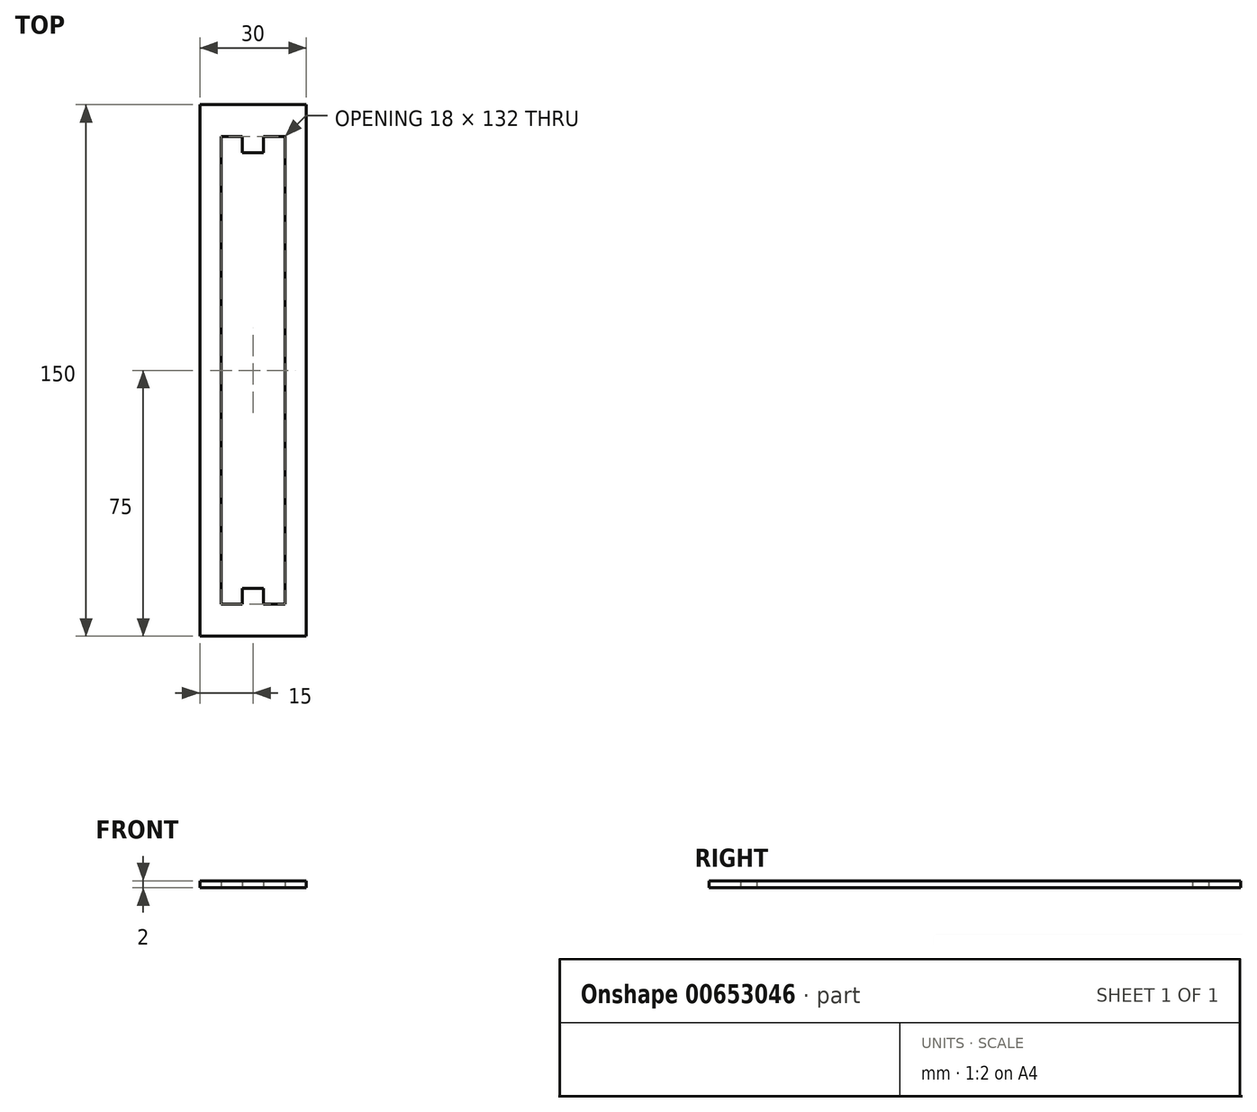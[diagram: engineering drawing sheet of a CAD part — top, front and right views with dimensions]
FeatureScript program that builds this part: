
annotation { "Feature Type Name" : "Feature", "Feature Type Description" : "" }
export const myFeature = defineFeature(function(context is Context, id is Id, definition is map)
    precondition{}
    {
        {
            var Q0;
            Q0=qCreatedBy(makeId("Top.planeOp"),FACE);
            var sketch = newSketch(context, id + "F0", { "sketchPlane" : qUnion([Q0])});
            skLineSegment(sketch, "E0.bottom", {"start": v(0, 0) * mm, "end": v(30, 0) * mm});
            skLineSegment(sketch, "E0.top", {"start": v(0, 150) * mm, "end": v(30, 150) * mm});
            skLineSegment(sketch, "E0.left", {"start": v(0, 0) * mm, "end": v(0, 150) * mm});
            skLineSegment(sketch, "E0.right", {"start": v(30, 0) * mm, "end": v(30, 150) * mm});
            skLineSegment(sketch, "E1", {"start": v(6, 141) * mm, "end": v(12, 141) * mm});
            skLineSegment(sketch, "E2", {"start": v(24, 141) * mm, "end": v(24, 9) * mm});
            skLineSegment(sketch, "E3", {"start": v(6, 141) * mm, "end": v(6, 9) * mm});
            skLineSegment(sketch, "E4", {"start": v(6, 9) * mm, "end": v(12, 9) * mm});
            skLineSegment(sketch, "E5", {"start": v(18, 141) * mm, "end": v(18, 136.5) * mm});
            skLineSegment(sketch, "E6", {"start": v(18, 136.5) * mm, "end": v(12, 136.5) * mm});
            skLineSegment(sketch, "E7", {"start": v(12, 136.5) * mm, "end": v(12, 141) * mm});
            skLineSegment(sketch, "E8", {"start": v(12, 9) * mm, "end": v(12, 13.5) * mm});
            skLineSegment(sketch, "E9", {"start": v(12, 13.5) * mm, "end": v(18, 13.5) * mm});
            skLineSegment(sketch, "E10", {"start": v(18, 13.5) * mm, "end": v(18, 9) * mm});
            skLineSegment(sketch, "E11.trimOffspring", {"start": v(18, 9) * mm, "end": v(24, 9) * mm});
            skLineSegment(sketch, "E12.trimOffspring", {"start": v(18, 141) * mm, "end": v(24, 141) * mm});
            skSolve(sketch);
        }
        {
            var Q0;
            Q0=qSketchRegion(id+"F0",true);
            extrude(context, id + "F1", {"entities" : qUnion([Q0]), "depth" : 2 * mm, "offsetDistance" : 25 * mm});
        }
    });
